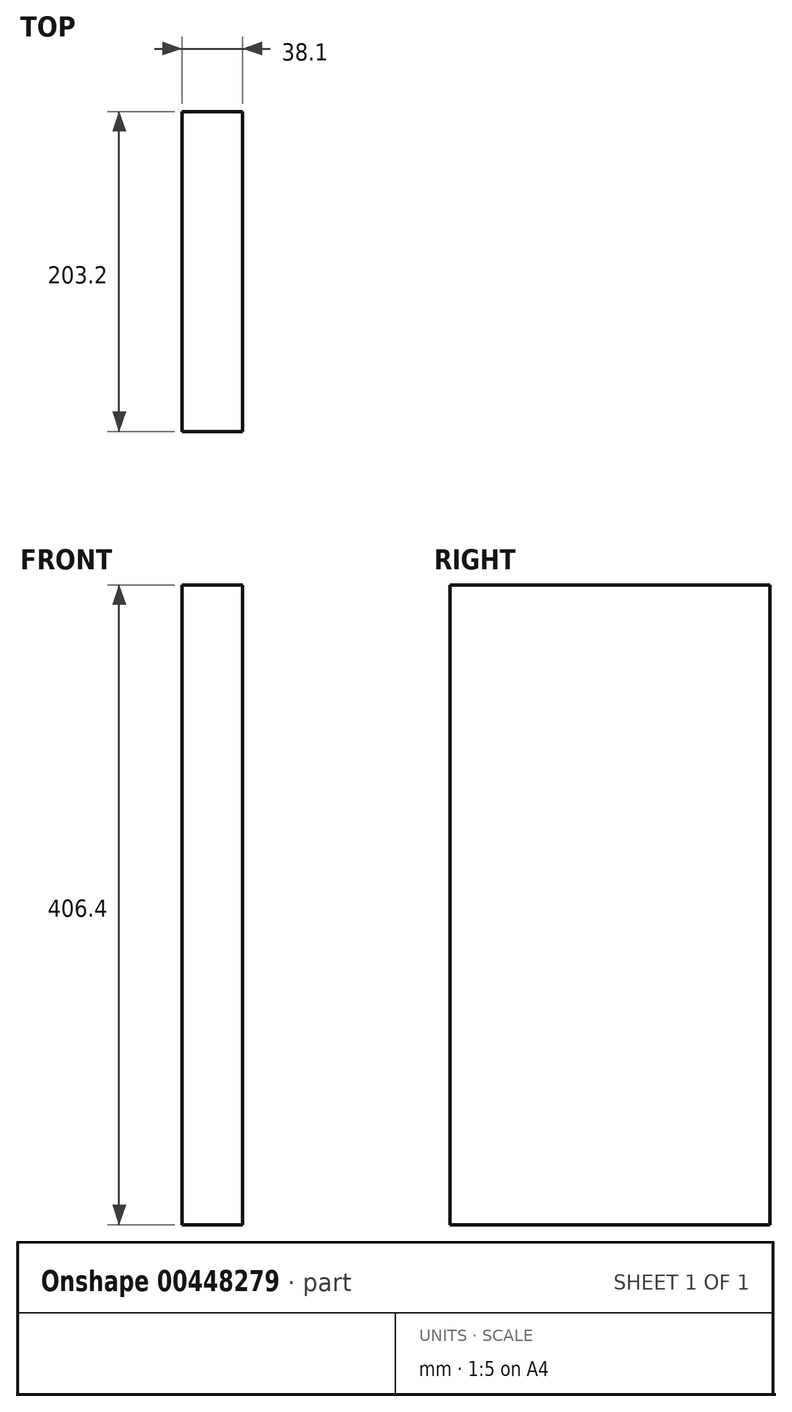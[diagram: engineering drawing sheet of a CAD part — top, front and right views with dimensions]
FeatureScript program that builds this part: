
annotation { "Feature Type Name" : "Feature", "Feature Type Description" : "" }
export const myFeature = defineFeature(function(context is Context, id is Id, definition is map)
    precondition{}
    {
        {
            var Q0;
            Q0=qCreatedBy(makeId("Right.planeOp"),FACE);
            var sketch = newSketch(context, id + "F0", { "sketchPlane" : qUnion([Q0])});
            skLineSegment(sketch, "E0.bottom", {"start": v(-203.2, 0) * mm, "end": v(0, 0) * mm});
            skLineSegment(sketch, "E0.top", {"start": v(-203.2, -406.4) * mm, "end": v(0, -406.4) * mm});
            skLineSegment(sketch, "E0.left", {"start": v(-203.2, 0) * mm, "end": v(-203.2, -406.4) * mm});
            skLineSegment(sketch, "E0.right", {"start": v(0, 0) * mm, "end": v(0, -406.4) * mm});
            skSolve(sketch);
        }
        {
            var Q0;
            Q0=makeQuery(id+"F0.imprint","IMPRINT",FACE,{"disambiguationData":[TD([[makeQuery(id+"F0.imprint","IMPRINT",EDGE,{"derivedFrom":sQuery(id+"F0.wireOp",EDGE,"E0.bottom")}),-1.0]])]});
            extrude(context, id + "F1", {"entities" : qUnion([Q0]), "oppositeDirection" : true, "depth" : 38.1 * mm});
        }
    });
